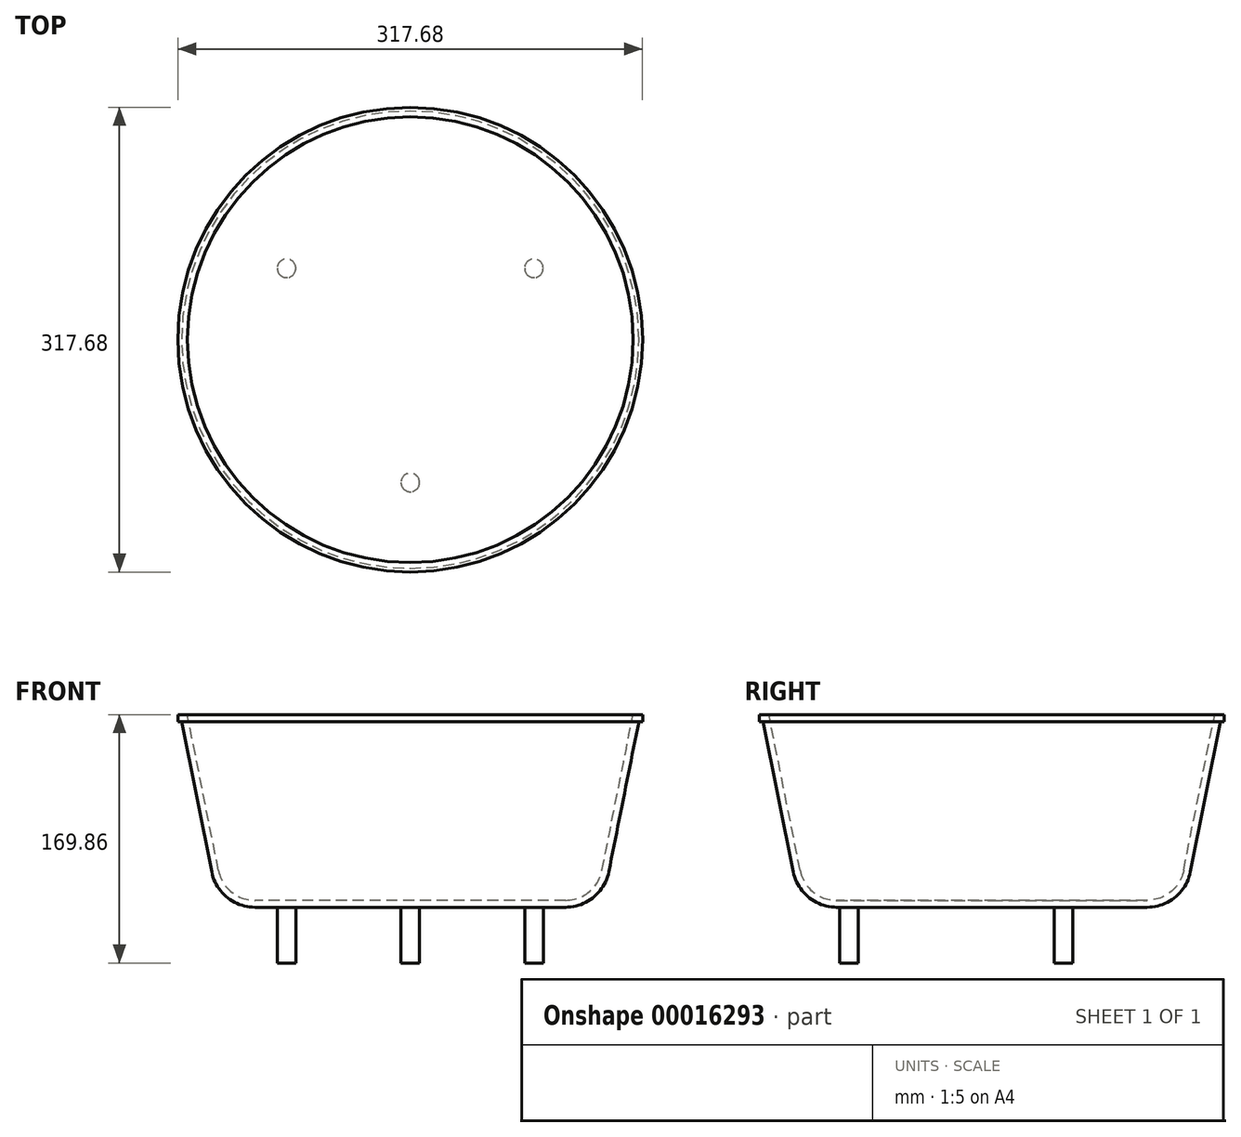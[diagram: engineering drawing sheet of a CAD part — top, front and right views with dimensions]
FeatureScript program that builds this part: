
annotation { "Feature Type Name" : "Feature", "Feature Type Description" : "" }
export const myFeature = defineFeature(function(context is Context, id is Id, definition is map)
    precondition{}
    {
        {
            var Q0;
            Q0=qCreatedBy(makeId("Front.planeOp"),FACE);
            var sketch = newSketch(context, id + "F0", { "sketchPlane" : qUnion([Q0])});
            skLineSegment(sketch, "E0", {"start": v(0, -127) * mm, "end": v(0, -131.76) * mm});
            skLineSegment(sketch, "E1", {"start": v(0, -127) * mm, "end": v(-106.18, -127) * mm});
            skLineSegment(sketch, "E2", {"start": v(-152.4, 0) * mm, "end": v(-131.08, -106.58) * mm});
            skPoint(sketch, "E3.visualSharp", {"position": v(-127, -127) * mm});
            skArc(sketch, "E3.filletArc", {"start": v(-131.08, -106.58) * mm, "mid": v(-122.28, -121.24) * mm, "end": v(-106.18, -127) * mm});
            skLineSegment(sketch, "E4.0", {"start": v(0, -131.76) * mm, "end": v(-106.18, -131.76) * mm});
            skArc(sketch, "E4.1", {"start": v(-135.75, -107.52) * mm, "mid": v(-125.3, -124.93) * mm, "end": v(-106.18, -131.76) * mm});
            skLineSegment(sketch, "E4.2", {"start": v(-156.3, -4.76) * mm, "end": v(-135.75, -107.52) * mm});
            skLineSegment(sketch, "E5", {"start": v(-152.4, 0) * mm, "end": v(-157.26, 0) * mm});
            skLineSegment(sketch, "E6", {"start": v(-157.26, 0) * mm, "end": v(-158.84, 0) * mm});
            skLineSegment(sketch, "E7", {"start": v(-158.84, 0) * mm, "end": v(-158.84, -4.76) * mm});
            skLineSegment(sketch, "E8", {"start": v(-158.84, -4.76) * mm, "end": v(-156.3, -4.76) * mm});
            skSolve(sketch);
        }
        {
            var Q0;
            Q0=makeQuery(id+"F0.imprint","IMPRINT",FACE,{"disambiguationData":[TD([[makeQuery(id+"F0.imprint","IMPRINT",EDGE,{"derivedFrom":sQuery(id+"F0.wireOp",EDGE,"E0")}),-1.0]])]});
            var Q1;
            Q1=sQuery(id+"F0.wireOp",EDGE,"E0");
            revolve(context, id + "F1", {"entities" : qUnion([Q0]), "axis" : qUnion([Q1]), "revolveType" : RevolveType.FULL});
        }
        {
            var Q0;
            Q0=makeQuery(id+"F1.opRevolve","SWEPT_FACE",FACE,{"disambiguationData":[OSD([sQuery(id+"F0.wireOp",EDGE,"E4.0")])]});
            var sketch = newSketch(context, id + "F2", { "sketchPlane" : qUnion([Q0])});
            skCircle(sketch, "E9", {"center": v(0, 97.65) * mm, "radius": 6.35 * mm});
            skCircle(sketch, "E10.1.0", {"center": v(-84.57, -48.83) * mm, "radius": 6.35 * mm});
            skCircle(sketch, "E10.2.0", {"center": v(84.57, -48.83) * mm, "radius": 6.35 * mm});
            skPoint(sketch, "E10.center", {"position": v(0, 0) * mm});
            skSolve(sketch);
        }
        {
            var Q0;
            Q0=makeQuery(id+"F2.imprint","IMPRINT",FACE,{"disambiguationData":[TD([[makeQuery(id+"F2.imprint","IMPRINT",EDGE,{"derivedFrom":sQuery(id+"F2.wireOp",EDGE,"E9")}),1.0]])]});
            var Q1;
            Q1=makeQuery(id+"F2.imprint","IMPRINT",FACE,{"disambiguationData":[TD([[makeQuery(id+"F2.imprint","IMPRINT",EDGE,{"derivedFrom":sQuery(id+"F2.wireOp",EDGE,"E10.2.0")}),1.0]])]});
            var Q2;
            Q2=makeQuery(id+"F2.imprint","IMPRINT",FACE,{"disambiguationData":[TD([[makeQuery(id+"F2.imprint","IMPRINT",EDGE,{"derivedFrom":sQuery(id+"F2.wireOp",EDGE,"E10.1.0")}),1.0]])]});
            extrude(context, id + "F3", {"entities" : qUnion([Q0, Q1, Q2]), "operationType" : NewBodyOperationType.ADD, "depth" : 38.1 * mm});
        }
    });
